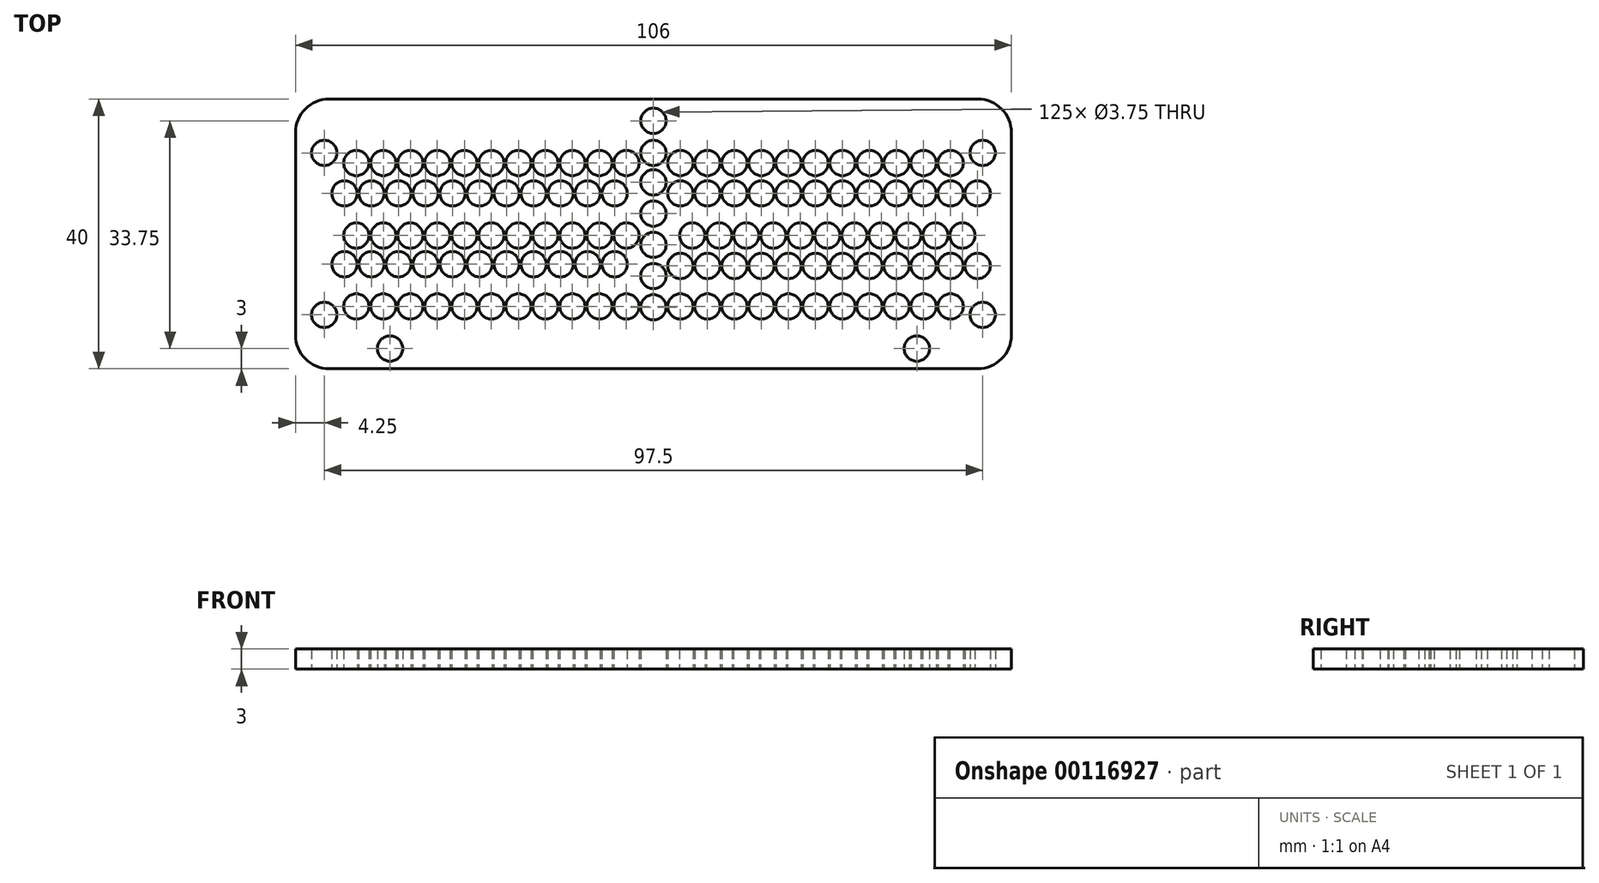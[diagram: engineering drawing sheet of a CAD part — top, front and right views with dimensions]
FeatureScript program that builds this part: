
annotation { "Feature Type Name" : "Feature", "Feature Type Description" : "" }
export const myFeature = defineFeature(function(context is Context, id is Id, definition is map)
    precondition{}
    {
        {
            var Q0;
            Q0=qCreatedBy(makeId("Top.planeOp"),FACE);
            var sketch = newSketch(context, id + "F0", { "sketchPlane" : qUnion([Q0])});
            skCircle(sketch, "E0", {"center": v(-48.75, 12) * mm, "radius": 1.88 * mm});
            skCircle(sketch, "E1", {"center": v(0, 12) * mm, "radius": 1.88 * mm});
            skCircle(sketch, "E2.MirrorC", {"center": v(-48.75, -12) * mm, "radius": 1.88 * mm});
            skCircle(sketch, "E3.MirrorC", {"center": v(48.75, 12) * mm, "radius": 1.88 * mm});
            skCircle(sketch, "E4.MirrorC", {"center": v(48.75, -12) * mm, "radius": 1.88 * mm});
            skCircle(sketch, "E5", {"center": v(0, 16.75) * mm, "radius": 1.88 * mm});
            skCircle(sketch, "E6", {"center": v(-4, 10.5) * mm, "radius": 1.88 * mm});
            skCircle(sketch, "E7", {"center": v(-5.75, 6) * mm, "radius": 1.88 * mm});
            skCircle(sketch, "E8.1.0.0", {"center": v(48, 6) * mm, "radius": 1.88 * mm});
            skLineSegment(sketch, "E8.direction1", {"start": v(-5.75, 6) * mm, "end": v(48, 6) * mm, "construction": true});
            skCircle(sketch, "E9.1.0.0", {"center": v(44, 10.5) * mm, "radius": 1.88 * mm});
            skLineSegment(sketch, "E9.direction1", {"start": v(-4, 10.5) * mm, "end": v(44, 10.5) * mm, "construction": true});
            skCircle(sketch, "E10.0.1.0", {"center": v(-5.75, -4.5) * mm, "radius": 1.88 * mm});
            skLineSegment(sketch, "E10.direction1", {"start": v(-5.75, 6) * mm, "end": v(19.25, 6) * mm, "construction": true});
            skLineSegment(sketch, "E10.direction2", {"start": v(-5.75, 6) * mm, "end": v(-5.75, -4.5) * mm, "construction": true});
            skCircle(sketch, "E11.0.1.0", {"center": v(-4, -0.25) * mm, "radius": 1.88 * mm});
            skLineSegment(sketch, "E11.direction1", {"start": v(-4, 10.5) * mm, "end": v(21, 10.5) * mm, "construction": true});
            skLineSegment(sketch, "E11.direction2", {"start": v(-4, 10.5) * mm, "end": v(-4, -0.25) * mm, "construction": true});
            skCircle(sketch, "E12.0.1.0", {"center": v(-4, -10.75) * mm, "radius": 1.88 * mm});
            skLineSegment(sketch, "E12.direction1", {"start": v(-4, -0.25) * mm, "end": v(21, -0.25) * mm, "construction": true});
            skLineSegment(sketch, "E12.direction2", {"start": v(-4, -0.25) * mm, "end": v(-4, -10.75) * mm, "construction": true});
            skCircle(sketch, "E13.0.1.0", {"center": v(48, -4.75) * mm, "radius": 1.88 * mm});
            skLineSegment(sketch, "E13.direction1", {"start": v(48, 6) * mm, "end": v(73, 6) * mm, "construction": true});
            skLineSegment(sketch, "E13.direction2", {"start": v(48, 6) * mm, "end": v(48, -4.75) * mm, "construction": true});
            skCircle(sketch, "E14.0.1.0", {"center": v(44, -10.75) * mm, "radius": 1.88 * mm});
            skLineSegment(sketch, "E14.direction1", {"start": v(44, 10.5) * mm, "end": v(69, 10.5) * mm, "construction": true});
            skLineSegment(sketch, "E14.direction2", {"start": v(44, 10.5) * mm, "end": v(44, -10.75) * mm, "construction": true});
            skCircle(sketch, "E15.1.0.0", {"center": v(45.75, -0.25) * mm, "radius": 1.88 * mm});
            skLineSegment(sketch, "E15.direction1", {"start": v(-4, -0.25) * mm, "end": v(45.75, -0.25) * mm, "construction": true});
            skCircle(sketch, "E16.1.0.0", {"center": v(-8, 10.5) * mm, "radius": 1.88 * mm});
            skCircle(sketch, "E16.1.0.1", {"center": v(-9.75, 6) * mm, "radius": 1.88 * mm});
            skCircle(sketch, "E16.1.0.2", {"center": v(-8, -0.25) * mm, "radius": 1.88 * mm});
            skCircle(sketch, "E16.1.0.3", {"center": v(-9.75, -4.5) * mm, "radius": 1.88 * mm});
            skCircle(sketch, "E16.1.0.4", {"center": v(-8, -10.75) * mm, "radius": 1.88 * mm});
            skCircle(sketch, "E16.1.0.5", {"center": v(40, 10.5) * mm, "radius": 1.88 * mm});
            skCircle(sketch, "E16.1.0.6", {"center": v(44, 6) * mm, "radius": 1.88 * mm});
            skCircle(sketch, "E16.1.0.7", {"center": v(41.75, -0.25) * mm, "radius": 1.88 * mm});
            skCircle(sketch, "E16.1.0.8", {"center": v(44, -4.75) * mm, "radius": 1.88 * mm});
            skCircle(sketch, "E16.1.0.9", {"center": v(40, -10.75) * mm, "radius": 1.88 * mm});
            skCircle(sketch, "E16.2.0.0", {"center": v(-12, 10.5) * mm, "radius": 1.88 * mm});
            skCircle(sketch, "E16.2.0.1", {"center": v(-13.75, 6) * mm, "radius": 1.88 * mm});
            skCircle(sketch, "E16.2.0.2", {"center": v(-12, -0.25) * mm, "radius": 1.88 * mm});
            skCircle(sketch, "E16.2.0.3", {"center": v(-13.75, -4.5) * mm, "radius": 1.88 * mm});
            skCircle(sketch, "E16.2.0.4", {"center": v(-12, -10.75) * mm, "radius": 1.88 * mm});
            skCircle(sketch, "E16.2.0.5", {"center": v(36, 10.5) * mm, "radius": 1.88 * mm});
            skCircle(sketch, "E16.2.0.6", {"center": v(40, 6) * mm, "radius": 1.88 * mm});
            skCircle(sketch, "E16.2.0.7", {"center": v(37.75, -0.25) * mm, "radius": 1.88 * mm});
            skCircle(sketch, "E16.2.0.8", {"center": v(40, -4.75) * mm, "radius": 1.88 * mm});
            skCircle(sketch, "E16.2.0.9", {"center": v(36, -10.75) * mm, "radius": 1.88 * mm});
            skCircle(sketch, "E16.3.0.0", {"center": v(-16, 10.5) * mm, "radius": 1.88 * mm});
            skCircle(sketch, "E16.3.0.1", {"center": v(-17.75, 6) * mm, "radius": 1.88 * mm});
            skCircle(sketch, "E16.3.0.2", {"center": v(-16, -0.25) * mm, "radius": 1.88 * mm});
            skCircle(sketch, "E16.3.0.3", {"center": v(-17.75, -4.5) * mm, "radius": 1.88 * mm});
            skCircle(sketch, "E16.3.0.4", {"center": v(-16, -10.75) * mm, "radius": 1.88 * mm});
            skCircle(sketch, "E16.3.0.5", {"center": v(32, 10.5) * mm, "radius": 1.88 * mm});
            skCircle(sketch, "E16.3.0.6", {"center": v(36, 6) * mm, "radius": 1.88 * mm});
            skCircle(sketch, "E16.3.0.7", {"center": v(33.75, -0.25) * mm, "radius": 1.88 * mm});
            skCircle(sketch, "E16.3.0.8", {"center": v(36, -4.75) * mm, "radius": 1.88 * mm});
            skCircle(sketch, "E16.3.0.9", {"center": v(32, -10.75) * mm, "radius": 1.88 * mm});
            skCircle(sketch, "E16.4.0.0", {"center": v(-20, 10.5) * mm, "radius": 1.88 * mm});
            skCircle(sketch, "E16.4.0.1", {"center": v(-21.75, 6) * mm, "radius": 1.88 * mm});
            skCircle(sketch, "E16.4.0.2", {"center": v(-20, -0.25) * mm, "radius": 1.88 * mm});
            skCircle(sketch, "E16.4.0.3", {"center": v(-21.75, -4.5) * mm, "radius": 1.88 * mm});
            skCircle(sketch, "E16.4.0.4", {"center": v(-20, -10.75) * mm, "radius": 1.88 * mm});
            skCircle(sketch, "E16.4.0.5", {"center": v(28, 10.5) * mm, "radius": 1.88 * mm});
            skCircle(sketch, "E16.4.0.6", {"center": v(32, 6) * mm, "radius": 1.88 * mm});
            skCircle(sketch, "E16.4.0.7", {"center": v(29.75, -0.25) * mm, "radius": 1.88 * mm});
            skCircle(sketch, "E16.4.0.8", {"center": v(32, -4.75) * mm, "radius": 1.88 * mm});
            skCircle(sketch, "E16.4.0.9", {"center": v(28, -10.75) * mm, "radius": 1.88 * mm});
            skCircle(sketch, "E16.5.0.0", {"center": v(-24, 10.5) * mm, "radius": 1.88 * mm});
            skCircle(sketch, "E16.5.0.1", {"center": v(-25.75, 6) * mm, "radius": 1.88 * mm});
            skCircle(sketch, "E16.5.0.2", {"center": v(-24, -0.25) * mm, "radius": 1.88 * mm});
            skCircle(sketch, "E16.5.0.3", {"center": v(-25.75, -4.5) * mm, "radius": 1.88 * mm});
            skCircle(sketch, "E16.5.0.4", {"center": v(-24, -10.75) * mm, "radius": 1.88 * mm});
            skCircle(sketch, "E16.5.0.5", {"center": v(24, 10.5) * mm, "radius": 1.88 * mm});
            skCircle(sketch, "E16.5.0.6", {"center": v(28, 6) * mm, "radius": 1.88 * mm});
            skCircle(sketch, "E16.5.0.7", {"center": v(25.75, -0.25) * mm, "radius": 1.88 * mm});
            skCircle(sketch, "E16.5.0.8", {"center": v(28, -4.75) * mm, "radius": 1.88 * mm});
            skCircle(sketch, "E16.5.0.9", {"center": v(24, -10.75) * mm, "radius": 1.88 * mm});
            skCircle(sketch, "E16.6.0.0", {"center": v(-28, 10.5) * mm, "radius": 1.88 * mm});
            skCircle(sketch, "E16.6.0.1", {"center": v(-29.75, 6) * mm, "radius": 1.88 * mm});
            skCircle(sketch, "E16.6.0.2", {"center": v(-28, -0.25) * mm, "radius": 1.88 * mm});
            skCircle(sketch, "E16.6.0.3", {"center": v(-29.75, -4.5) * mm, "radius": 1.88 * mm});
            skCircle(sketch, "E16.6.0.4", {"center": v(-28, -10.75) * mm, "radius": 1.88 * mm});
            skCircle(sketch, "E16.6.0.5", {"center": v(20, 10.5) * mm, "radius": 1.88 * mm});
            skCircle(sketch, "E16.6.0.6", {"center": v(24, 6) * mm, "radius": 1.88 * mm});
            skCircle(sketch, "E16.6.0.7", {"center": v(21.75, -0.25) * mm, "radius": 1.88 * mm});
            skCircle(sketch, "E16.6.0.8", {"center": v(24, -4.75) * mm, "radius": 1.88 * mm});
            skCircle(sketch, "E16.6.0.9", {"center": v(20, -10.75) * mm, "radius": 1.88 * mm});
            skCircle(sketch, "E16.7.0.0", {"center": v(-32, 10.5) * mm, "radius": 1.88 * mm});
            skCircle(sketch, "E16.7.0.1", {"center": v(-33.75, 6) * mm, "radius": 1.88 * mm});
            skCircle(sketch, "E16.7.0.2", {"center": v(-32, -0.25) * mm, "radius": 1.88 * mm});
            skCircle(sketch, "E16.7.0.3", {"center": v(-33.75, -4.5) * mm, "radius": 1.88 * mm});
            skCircle(sketch, "E16.7.0.4", {"center": v(-32, -10.75) * mm, "radius": 1.88 * mm});
            skCircle(sketch, "E16.7.0.5", {"center": v(16, 10.5) * mm, "radius": 1.88 * mm});
            skCircle(sketch, "E16.7.0.6", {"center": v(20, 6) * mm, "radius": 1.88 * mm});
            skCircle(sketch, "E16.7.0.7", {"center": v(17.75, -0.25) * mm, "radius": 1.88 * mm});
            skCircle(sketch, "E16.7.0.8", {"center": v(20, -4.75) * mm, "radius": 1.88 * mm});
            skCircle(sketch, "E16.7.0.9", {"center": v(16, -10.75) * mm, "radius": 1.88 * mm});
            skCircle(sketch, "E16.8.0.0", {"center": v(-36, 10.5) * mm, "radius": 1.88 * mm});
            skCircle(sketch, "E16.8.0.1", {"center": v(-37.75, 6) * mm, "radius": 1.88 * mm});
            skCircle(sketch, "E16.8.0.2", {"center": v(-36, -0.25) * mm, "radius": 1.88 * mm});
            skCircle(sketch, "E16.8.0.3", {"center": v(-37.75, -4.5) * mm, "radius": 1.88 * mm});
            skCircle(sketch, "E16.8.0.4", {"center": v(-36, -10.75) * mm, "radius": 1.88 * mm});
            skCircle(sketch, "E16.8.0.5", {"center": v(12, 10.5) * mm, "radius": 1.88 * mm});
            skCircle(sketch, "E16.8.0.6", {"center": v(16, 6) * mm, "radius": 1.88 * mm});
            skCircle(sketch, "E16.8.0.7", {"center": v(13.75, -0.25) * mm, "radius": 1.88 * mm});
            skCircle(sketch, "E16.8.0.8", {"center": v(16, -4.75) * mm, "radius": 1.88 * mm});
            skCircle(sketch, "E16.8.0.9", {"center": v(12, -10.75) * mm, "radius": 1.88 * mm});
            skCircle(sketch, "E16.9.0.0", {"center": v(-40, 10.5) * mm, "radius": 1.88 * mm});
            skCircle(sketch, "E16.9.0.1", {"center": v(-41.75, 6) * mm, "radius": 1.88 * mm});
            skCircle(sketch, "E16.9.0.2", {"center": v(-40, -0.25) * mm, "radius": 1.88 * mm});
            skCircle(sketch, "E16.9.0.3", {"center": v(-41.75, -4.5) * mm, "radius": 1.88 * mm});
            skCircle(sketch, "E16.9.0.4", {"center": v(-40, -10.75) * mm, "radius": 1.88 * mm});
            skCircle(sketch, "E16.9.0.5", {"center": v(8, 10.5) * mm, "radius": 1.88 * mm});
            skCircle(sketch, "E16.9.0.6", {"center": v(12, 6) * mm, "radius": 1.88 * mm});
            skCircle(sketch, "E16.9.0.7", {"center": v(9.75, -0.25) * mm, "radius": 1.88 * mm});
            skCircle(sketch, "E16.9.0.8", {"center": v(12, -4.75) * mm, "radius": 1.88 * mm});
            skCircle(sketch, "E16.9.0.9", {"center": v(8, -10.75) * mm, "radius": 1.88 * mm});
            skCircle(sketch, "E16.10.0.0", {"center": v(-44, 10.5) * mm, "radius": 1.88 * mm});
            skCircle(sketch, "E16.10.0.1", {"center": v(-45.75, 6) * mm, "radius": 1.88 * mm});
            skCircle(sketch, "E16.10.0.2", {"center": v(-44, -0.25) * mm, "radius": 1.88 * mm});
            skCircle(sketch, "E16.10.0.3", {"center": v(-45.75, -4.5) * mm, "radius": 1.88 * mm});
            skCircle(sketch, "E16.10.0.4", {"center": v(-44, -10.75) * mm, "radius": 1.88 * mm});
            skCircle(sketch, "E16.10.0.5", {"center": v(4, 10.5) * mm, "radius": 1.88 * mm});
            skCircle(sketch, "E16.10.0.6", {"center": v(8, 6) * mm, "radius": 1.88 * mm});
            skCircle(sketch, "E16.10.0.7", {"center": v(5.75, -0.25) * mm, "radius": 1.88 * mm});
            skCircle(sketch, "E16.10.0.8", {"center": v(8, -4.75) * mm, "radius": 1.88 * mm});
            skCircle(sketch, "E16.10.0.9", {"center": v(4, -10.75) * mm, "radius": 1.88 * mm});
            skLineSegment(sketch, "E16.direction1", {"start": v(-4, -10.75) * mm, "end": v(-8, -10.75) * mm, "construction": true});
            skCircle(sketch, "E17", {"center": v(0, -10.88) * mm, "radius": 1.88 * mm});
            skCircle(sketch, "E18.0.1.0", {"center": v(0, -6.25) * mm, "radius": 1.88 * mm});
            skCircle(sketch, "E18.0.2.0", {"center": v(0, -1.63) * mm, "radius": 1.88 * mm});
            skCircle(sketch, "E18.0.3.0", {"center": v(0, 3) * mm, "radius": 1.88 * mm});
            skCircle(sketch, "E18.0.4.0", {"center": v(0, 7.62) * mm, "radius": 1.88 * mm});
            skLineSegment(sketch, "E18.direction1", {"start": v(0, -10.88) * mm, "end": v(25, -10.88) * mm, "construction": true});
            skLineSegment(sketch, "E18.direction2", {"start": v(0, -10.88) * mm, "end": v(0, -6.25) * mm, "construction": true});
            skCircle(sketch, "E19.1.0.0", {"center": v(4, 6) * mm, "radius": 1.88 * mm});
            skCircle(sketch, "E19.1.0.1", {"center": v(4, -4.75) * mm, "radius": 1.88 * mm});
            skLineSegment(sketch, "E19.direction1", {"start": v(8, -4.75) * mm, "end": v(4, -4.75) * mm, "construction": true});
            skCircle(sketch, "E20", {"center": v(-39, -17) * mm, "radius": 1.88 * mm});
            skCircle(sketch, "E21.MirrorC", {"center": v(39, -17) * mm, "radius": 1.88 * mm});
            skLineSegment(sketch, "E22.bottom", {"start": v(48, -20) * mm, "end": v(-48, -20) * mm});
            skLineSegment(sketch, "E22.top", {"start": v(48, 20) * mm, "end": v(-48, 20) * mm});
            skLineSegment(sketch, "E22.left", {"start": v(53, -15) * mm, "end": v(53, 15) * mm});
            skLineSegment(sketch, "E22.right", {"start": v(-53, -15) * mm, "end": v(-53, 15) * mm});
            skPoint(sketch, "E22.middle", {"position": v(0, 0) * mm});
            skPoint(sketch, "E23.visualSharp", {"position": v(-53, 20) * mm});
            skArc(sketch, "E23.filletArc", {"start": v(-48, 20) * mm, "mid": v(-51.54, 18.54) * mm, "end": v(-53, 15) * mm});
            skPoint(sketch, "E24.visualSharp", {"position": v(-53, -20) * mm});
            skArc(sketch, "E24.filletArc", {"start": v(-53, -15) * mm, "mid": v(-51.54, -18.54) * mm, "end": v(-48, -20) * mm});
            skPoint(sketch, "E25.visualSharp", {"position": v(53, -20) * mm});
            skArc(sketch, "E25.filletArc", {"start": v(48, -20) * mm, "mid": v(51.54, -18.54) * mm, "end": v(53, -15) * mm});
            skPoint(sketch, "E26.visualSharp", {"position": v(53, 20) * mm});
            skArc(sketch, "E26.filletArc", {"start": v(53, 15) * mm, "mid": v(51.54, 18.54) * mm, "end": v(48, 20) * mm});
            skSolve(sketch);
        }
        {
            var Q0;
            Q0=makeQuery(id+"F0.imprint","IMPRINT",FACE,{"disambiguationData":[TD([[makeQuery(id+"F0.imprint","IMPRINT",EDGE,{"derivedFrom":sQuery(id+"F0.wireOp",EDGE,"E0")}),-1.0]])]});
            extrude(context, id + "F1", {"entities" : qUnion([Q0]), "depth" : 3 * mm});
        }
    });
